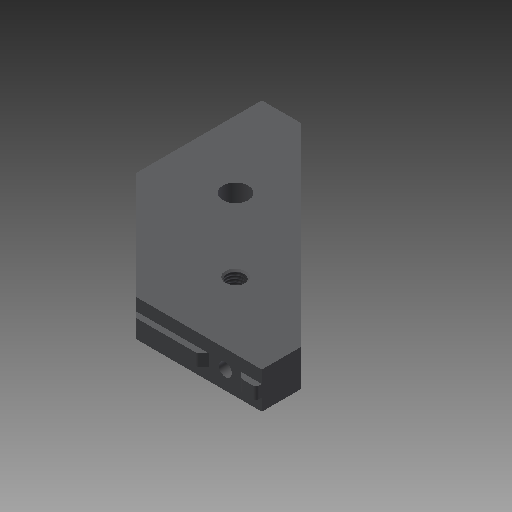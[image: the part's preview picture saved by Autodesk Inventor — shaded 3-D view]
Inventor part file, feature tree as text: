
AUTODESK INVENTOR PART (.ipt)
format: ipt  version: 2018 (Build 220112000, 112)  size: 205,312 bytes
history: native  units: mm
features: other x56, sketch x11, extrude x8, hole x2, revolve x1
ambient origin geometry x8: Origin, YZ Plane, XZ Plane, XY Plane, X Axis, Y Axis, Z Axis, Center Point
bodies: Solid1 (feature_tree)
feature tree (78):
  extrude  "Extrusion1"  Depth=8.0mm TaperAngle=0.0deg
  extrude  "Extrusion2"  Depth=8.0mm TaperAngle=0.0deg
  extrude  "Extrusion3"  TaperAngle=360.0deg  [1 undecoded]
  extrude  "Extrusion4"  Depth=10.0mm TaperAngle=0.0deg
  extrude  "Extrusion5"  [1 undecoded]
  hole  "Drilling 1"  [1 undecoded]
  revolve  "Revolution1"  [1 undecoded]
  extrude  "Extrusion6"  [1 undecoded]
  hole  "Drilling 3"  [1 undecoded]
  extrude  "Extrusion7"  [1 undecoded]
  extrude  "Extrusion8"  [1 undecoded]
  other  "side_2a_XY"
  other  "side_2a_YZ"
  other  "side_2a_ZX"
  other  "side_2a_X"
  other  "side_2a_Y"
  other  "side_2a_Z"
  other  "side_2a_Center"
  other  "side_2b_XY"
  other  "side_2b_YZ"
  other  "side_2b_ZX"
  other  "side_2b_X"
  other  "side_2b_Y"
  other  "side_2b_Z"
  other  "side_2b_Center"
  other  "side_5a_XY"
  other  "side_5a_YZ"
  other  "side_5a_ZX"
  other  "side_5a_X"
  other  "side_5a_Y"
  other  "side_5a_Z"
  other  "side_5a_Center"
  other  "side_5b_XY"
  other  "side_5b_YZ"
  other  "side_5b_ZX"
  other  "side_5b_X"
  other  "side_5b_Y"
  other  "side_5b_Z"
  other  "side_5b_Center"
  other  "side_1a_XY"
  other  "side_1a_YZ"
  other  "side_1a_ZX"
  other  "side_1a_X"
  other  "side_1a_Y"
  other  "side_1a_Z"
  other  "side_1a_Center"
  other  "side_1b_XY"
  other  "side_1b_YZ"
  other  "side_1b_ZX"
  other  "side_1b_X"
  other  "side_1b_Y"
  other  "side_1b_Z"
  other  "side_1b_Center"
  other  "side_6a_XY"
  other  "side_6a_YZ"
  other  "side_6a_ZX"
  other  "side_6a_X"
  other  "side_6a_Y"
  other  "side_6a_Z"
  other  "side_6a_Center"
  other  "side_6b_XY"
  other  "side_6b_YZ"
  other  "side_6b_ZX"
  other  "side_6b_X"
  other  "side_6b_Y"
  other  "side_6b_Z"
  other  "side_6b_Center"
  sketch  "Skizze_1"  dims[d0=25.0mm d1=0.0mm d2=8.0mm d3=0.0mm]
  sketch  "Skizze_2"  dims[d4=8.0mm d5=0.0mm d6=8.0mm d7=0.0mm]
  sketch  "Skizze_3"  dims[d8=8.0mm d9=0.0mm]
  sketch  "Skizze_4"  dims[d10=9.0mm d11=6.0mm d12=4.0mm d13=2.0mm d14=90.0deg d15=92.340434mm d16=0.0mm d17=360.0deg]
  sketch  "Skizze_5"  dims[d18=10.0mm d19=0.0mm]
  sketch  "Sketch6"  dims[d20=11.835mm d21=25.0mm d22=14.0mm d23=2.0mm d24=15.707963mm d25=25.0mm d26=0.0mm d27=10.0mm d28=0.0mm]
  sketch  "Skizze_7"  dims[d29=10.0mm d30=0.0mm]
  sketch  "Skizze_8"
  sketch  "Sketch9"
  sketch  "Skizze_10"
  sketch  "Skizze_11"
note: 8 required parameter values undecoded (feature->parameter linkage not recoverable at this tier; creation-order binding heuristic only, values carry confidence <= 0.55)
